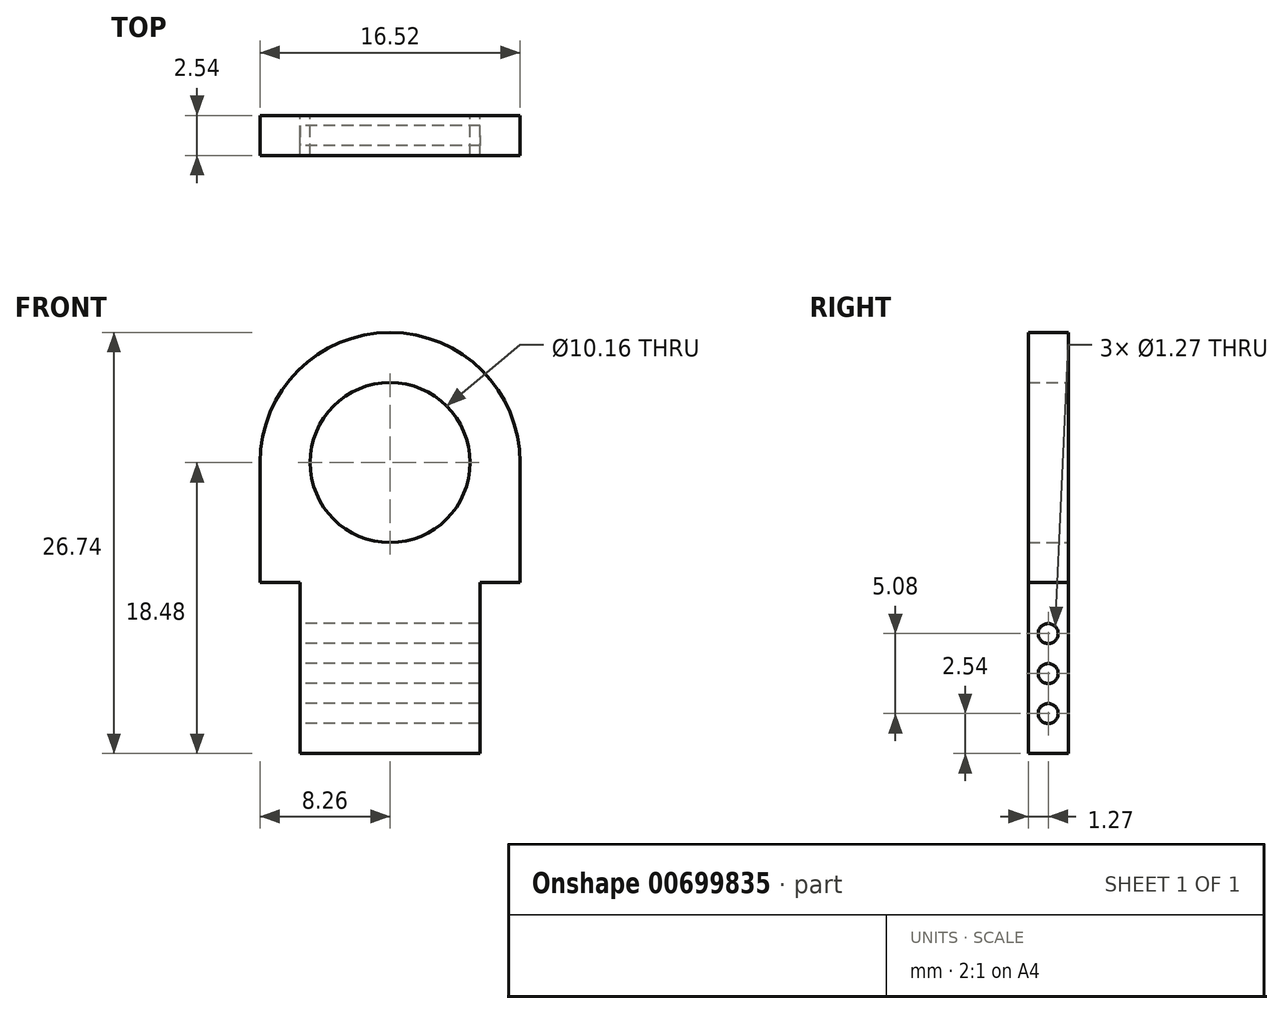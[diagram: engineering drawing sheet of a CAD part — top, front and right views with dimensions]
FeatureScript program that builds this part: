
annotation { "Feature Type Name" : "Feature", "Feature Type Description" : "" }
export const myFeature = defineFeature(function(context is Context, id is Id, definition is map)
    precondition{}
    {
        {
            var Q0;
            Q0=qCreatedBy(makeId("Front.planeOp"),FACE);
            var sketch = newSketch(context, id + "F0", { "sketchPlane" : qUnion([Q0])});
            skLineSegment(sketch, "E0.bottom", {"start": v(-18.45, 9) * mm, "end": v(-7.02, 9) * mm});
            skLineSegment(sketch, "E0.top", {"start": v(-18.45, -9.48) * mm, "end": v(-7.02, -9.48) * mm});
            skLineSegment(sketch, "E0.left", {"start": v(-18.45, 1.39) * mm, "end": v(-18.45, -9.48) * mm});
            skLineSegment(sketch, "E0.right", {"start": v(-7.02, 1.39) * mm, "end": v(-7.02, -9.48) * mm});
            skLineSegment(sketch, "E1.bottom", {"start": v(-18.45, 1.39) * mm, "end": v(-7.02, 1.39) * mm});
            skCircle(sketch, "E2", {"center": v(-12.74, 9) * mm, "radius": 5.08 * mm});
            skPoint(sketch, "E3.endSnap0", {"position": v(-7.02, -4.05) * mm});
            skLineSegment(sketch, "E4", {"start": v(-17.18, 1.39) * mm, "end": v(-7.17, 1.39) * mm});
            skLineSegment(sketch, "E5", {"start": v(-12.74, -9.48) * mm, "end": v(-12.74, -1.86) * mm});
            skPoint(sketch, "E6.orphan", {"position": v(-18.45, -1.86) * mm});
            skLineSegment(sketch, "E7", {"start": v(-18.45, 1.39) * mm, "end": v(-3.22, 1.39) * mm});
            skLineSegment(sketch, "E8", {"start": v(-3.22, 1.39) * mm, "end": v(-21, 1.39) * mm});
            skPoint(sketch, "E8.endSnap0", {"position": v(-12.18, 1.39) * mm});
            skLineSegment(sketch, "E9.bottom", {"start": v(-21, 1.39) * mm, "end": v(-4.48, 1.39) * mm});
            skLineSegment(sketch, "E9.top", {"start": v(-21, 9) * mm, "end": v(-4.48, 9) * mm});
            skLineSegment(sketch, "E9.left", {"start": v(-21, 1.39) * mm, "end": v(-21, 9) * mm});
            skLineSegment(sketch, "E9.right", {"start": v(-4.48, 1.39) * mm, "end": v(-4.48, 9) * mm});
            skLineSegment(sketch, "E10", {"start": v(-12.74, -9.48) * mm, "end": v(-12.74, 9) * mm});
            skArc(sketch, "E11.trimOffspring", {"start": v(-4.48, 9) * mm, "mid": v(-12.74, 17.26) * mm, "end": v(-21, 9) * mm});
            skPoint(sketch, "E12.center.orphan", {"position": v(-17.18, -6.94) * mm});
            skSolve(sketch);
        }
        {
            var Q0;
            Q0=qSketchRegion(id+"F0",true);
            extrude(context, id + "F1", {"entities" : qUnion([Q0]), "depth" : 2.54 * mm});
        }
        {
            var Q0;
            Q0=makeQuery(id+"F1.opExtrude","SWEPT_FACE",FACE,{"disambiguationData":[OSD([sQuery(id+"F0.wireOp",EDGE,"E0.left")])]});
            var sketch = newSketch(context, id + "F2", { "sketchPlane" : qUnion([Q0])});
            skLineSegment(sketch, "E13", {"start": v(1.27, -9.48) * mm, "end": v(1.27, 1.39) * mm});
            skLineSegment(sketch, "E14", {"start": v(0, -6.94) * mm, "end": v(2.54, -6.94) * mm});
            skLineSegment(sketch, "E15", {"start": v(2.54, -6.94) * mm, "end": v(2.54, -4.4) * mm});
            skLineSegment(sketch, "E16", {"start": v(2.54, -4.4) * mm, "end": v(0, -4.4) * mm});
            skLineSegment(sketch, "E17", {"start": v(0, -4.4) * mm, "end": v(0, -1.86) * mm});
            skLineSegment(sketch, "E18", {"start": v(0, -1.86) * mm, "end": v(2.54, -1.86) * mm});
            skCircle(sketch, "E19", {"center": v(1.27, -1.86) * mm, "radius": 0.64 * mm});
            skCircle(sketch, "E20", {"center": v(1.27, -4.4) * mm, "radius": 0.64 * mm});
            skCircle(sketch, "E21", {"center": v(1.27, -6.94) * mm, "radius": 0.64 * mm});
            skSolve(sketch);
        }
        {
            var Q0;
            Q0=sQuery(id+"F2.wireOp",VERTEX,"E19.center");
            var Q1;
            Q1=sQuery(id+"F2.wireOp",VERTEX,"E20.center");
            var Q2;
            Q2=sQuery(id+"F2.wireOp",VERTEX,"E21.center");
            var Q3;
            Q3=makeQuery(id+"F1.opExtrude","SWEPT_BODY",BODY,{"disambiguationData":[OSD([sQuery(id+"F0.wireOp",EDGE,"E0.top"),sQuery(id+"F0.wireOp",EDGE,"E0.left"),sQuery(id+"F0.wireOp",EDGE,"E0.right"),sQuery(id+"F0.wireOp",EDGE,"E2"),sQuery(id+"F0.wireOp",EDGE,"E9.bottom"),sQuery(id+"F0.wireOp",EDGE,"E9.left"),sQuery(id+"F0.wireOp",EDGE,"E9.right"),sQuery(id+"F0.wireOp",EDGE,"E11.trimOffspring")])]});
            hole(context, id + "F3", {"style" : HoleStyle.SIMPLE, "endStyle" : HoleEndStyle.BLIND, "holeDiameter" : 1.27 * mm, "holeDepth" : 25.4 * mm, "isTappedThrough" : true, "tappedDepth" : 12.7 * mm, "tapClearance" : 3, "locations" : qUnion([Q0, Q1, Q2]), "scope" : qUnion([Q3])});
        }
    });
